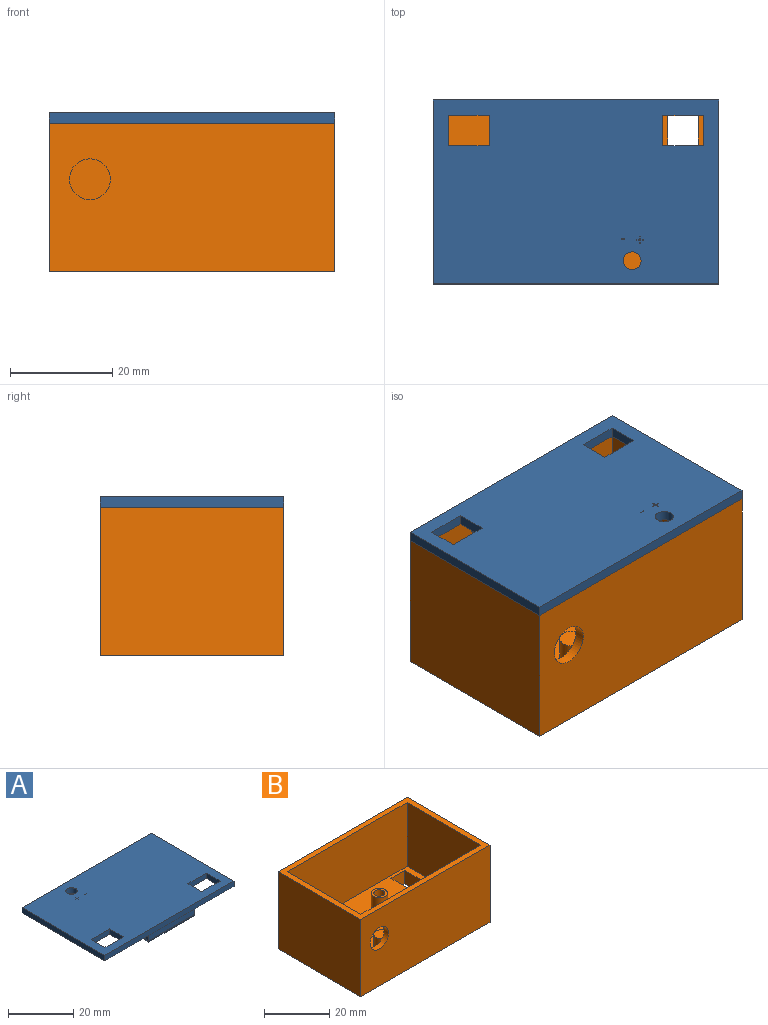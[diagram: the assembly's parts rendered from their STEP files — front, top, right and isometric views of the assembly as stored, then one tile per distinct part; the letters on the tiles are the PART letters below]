
ASSEMBLY  parts=2 mates=1
PART A: 47 faces, bbox 56x36x7 mm
  f0: plane 56x36mm, normal (0,0,1), area 1909.8mm2, adj f1,f2,f3,f4,f20,f21,f22,f23
  f1: plane 36x2mm, normal (-1,0,0), area 72mm2, adj f0,f2,f4,f5
  f2: plane 56x2mm, normal (0,-1,0), area 112mm2, adj f0,f1,f3,f5
  f3: plane 36x2mm, normal (1,0,0), area 72mm2, adj f0,f2,f4,f5
  f4: plane 56x2mm, normal (0,1,0), area 112mm2, adj f0,f1,f3,f5
  f5: plane 56x36mm, normal (0,0,-1), area 1840.4mm2, adj f1,f2,f3,f4,f6,f7,f8,f9
  f6: plane 4x2mm, normal (-1,0,0), area 8mm2, adj f5,f7,f9,f17
  f7: plane 20x4mm, normal (0,1,0), area 80mm2, adj f5,f6,f8,f18
  f8: plane 4x2mm, normal (1,0,0), area 8mm2, adj f5,f7,f9,f19
  f9: plane 20x4mm, normal (0,-1,0), area 80mm2, adj f5,f6,f8,f18
  f10: plane 15x4mm, normal (0,-1,0), area 60mm2, adj f5,f11,f13,f15
  f11: plane 4x2mm, normal (-1,0,0), area 8mm2, adj f5,f10,f12,f14
  f12: plane 15x4mm, normal (0,1,0), area 60mm2, adj f5,f11,f13,f15
  f13: plane 4x2mm, normal (1,0,0), area 8mm2, adj f5,f10,f12,f16
  f14: cylinder r=1mm len=2mm, axis (0,-1,0), area 2mm2, adj f11,f15
  f15: cylinder r=1mm len=15mm, axis (1,0,0), area 44.8mm2, adj f10,f12,f14,f16
  f16: cylinder r=1mm len=2mm, axis (0,1,0), area 2mm2, adj f13,f15
  f17: cylinder r=1mm len=2mm, axis (0,-1,0), area 2mm2, adj f6,f18
  f18: cylinder r=1mm len=20mm, axis (1,0,0), area 60.5mm2, adj f7,f9,f17,f19
  f19: cylinder r=1mm len=2mm, axis (0,1,0), area 2mm2, adj f8,f18
  f20: cylinder r=1.75mm len=3.5mm, axis (0,0,1), area 22mm2, adj f0,f5
  f21: plane 6x2mm, normal (1,0,0), area 12mm2, adj f0,f5,f22,f23
  f22: plane 8x2mm, normal (0,-1,0), area 16mm2, adj f0,f5,f21,f24
  f23: plane 8x2mm, normal (0,1,0), area 16mm2, adj f0,f5,f21,f24
  f24: plane 6x2mm, normal (-1,0,0), area 12mm2, adj f0,f5,f22,f23
  f25: plane 6x2mm, normal (1,0,0), area 12mm2, adj f0,f5,f26,f27
  f26: plane 8x2mm, normal (0,-1,0), area 16mm2, adj f0,f5,f25,f28
  f27: plane 8x2mm, normal (0,1,0), area 16mm2, adj f0,f5,f25,f28
  f28: plane 6x2mm, normal (-1,0,0), area 12mm2, adj f0,f5,f26,f27
  f29: plane 0.5x0.21mm, normal (1,0,0), area 0.1mm2, adj f0,f30,f32,f33
  f30: plane 0.67x0.5mm, normal (0,1,0), area 0.3mm2, adj f0,f29,f31,f33
  f31: plane 0.5x0.21mm, normal (-1,0,0), area 0.1mm2, adj f0,f30,f32,f33
  f32: plane 0.67x0.5mm, normal (0,-1,0), area 0.3mm2, adj f0,f29,f31,f33
  f33: plane 0.67x0.21mm, normal (0,0,1), area 0.1mm2, adj f29,f30,f31,f32
  f34: plane 0.56x0.5mm, normal (0,-1,0), area 0.3mm2, adj f0,f35,f45,f46
  f35: plane 0.58x0.5mm, normal (-1,0,0), area 0.3mm2, adj f0,f34,f36,f46
  f36: plane 0.5x0.19mm, normal (0,-1,0), area 0.1mm2, adj f0,f35,f37,f46
  f37: plane 0.58x0.5mm, normal (1,0,0), area 0.3mm2, adj f0,f36,f38,f46
  f38: plane 0.56x0.5mm, normal (0,-1,0), area 0.3mm2, adj f0,f37,f39,f46
  f39: plane 0.5x0.19mm, normal (1,0,0), area 0.1mm2, adj f0,f38,f40,f46
  f40: plane 0.56x0.5mm, normal (0,1,0), area 0.3mm2, adj f0,f39,f41,f46
  f41: plane 0.58x0.5mm, normal (1,0,0), area 0.3mm2, adj f0,f40,f42,f46
  f42: plane 0.5x0.19mm, normal (0,1,0), area 0.1mm2, adj f0,f41,f43,f46
  f43: plane 0.58x0.5mm, normal (-1,0,0), area 0.3mm2, adj f0,f42,f44,f46
  f44: plane 0.56x0.5mm, normal (0,1,0), area 0.3mm2, adj f0,f43,f45,f46
  f45: plane 0.5x0.19mm, normal (-1,0,0), area 0.1mm2, adj f0,f34,f44,f46
  f46: plane 1.35x1.3mm, normal (0,0,1), area 0.5mm2, adj f34,f35,f36,f37,f38,f39,f40,f41
PART B: 42 faces, bbox 56x36x29 mm
  f0: plane 52x32mm, normal (0,0,1), area 1525.1mm2, adj f7,f8,f9,f10,f25,f27,f29,f34
  f1: plane 56x36mm, normal (0,0,-1), area 1877.7mm2, adj f2,f3,f4,f5,f11,f12,f13,f14
  f2: plane 36x29mm, normal (-1,0,0), area 1044mm2, adj f1,f3,f5,f6
  f3: plane 56x29mm, normal (0,-1,0), area 1573.7mm2, adj f1,f2,f4,f6,f33
  f4: plane 36x29mm, normal (1,0,0), area 1044mm2, adj f1,f3,f5,f6
  f5: plane 56x29mm, normal (0,1,0), area 1624mm2, adj f1,f2,f4,f6
  f6: plane 56x36mm, normal (0,0,1), area 352mm2, adj f2,f3,f4,f5,f7,f8,f9,f10
  f7: plane 32x24mm, normal (1,0,0), area 768mm2, adj f0,f6,f8,f9
  f8: plane 52x24mm, normal (0,-1,0), area 1248mm2, adj f0,f6,f7,f10
  f9: plane 52x24mm, normal (0,1,0), area 1197.7mm2, adj f0,f6,f7,f10,f33
  f10: plane 32x24mm, normal (-1,0,0), area 768mm2, adj f0,f6,f8,f9
  f11: plane 3.35x3mm, normal (0,-1,0), area 10mm2, adj f1,f12,f16,f17
  f12: plane 3x2.9mm, normal (-0.87,-0.5,0), area 10mm2, adj f1,f11,f13,f17
  f13: plane 3x2.9mm, normal (-0.87,0.5,0), area 10mm2, adj f1,f12,f14,f17
  f14: plane 3.35x3mm, normal (0,1,0), area 10mm2, adj f1,f13,f15,f17
  f15: plane 3x2.9mm, normal (0.87,0.5,0), area 10mm2, adj f1,f14,f16,f17
  f16: plane 3x2.9mm, normal (0.87,-0.5,0), area 10mm2, adj f1,f11,f15,f17
  f17: plane 6.7x5.8mm, normal (0,0,-1), area 20.1mm2, adj f11,f12,f13,f14,f15,f16,f32
  f18: plane 3.35x3mm, normal (0,-1,0), area 10mm2, adj f1,f19,f23,f24
  f19: plane 3x2.9mm, normal (-0.87,-0.5,0), area 10mm2, adj f1,f18,f20,f24
  f20: plane 3x2.9mm, normal (-0.87,0.5,0), area 10mm2, adj f1,f19,f21,f24
  f21: plane 3.35x3mm, normal (0,1,0), area 10mm2, adj f1,f20,f22,f24
  f22: plane 3x2.9mm, normal (0.87,0.5,0), area 10mm2, adj f1,f21,f23,f24
  f23: plane 3x2.9mm, normal (0.87,-0.5,0), area 10mm2, adj f1,f18,f22,f24
  f24: plane 6.7x5.8mm, normal (0,0,-1), area 20.1mm2, adj f18,f19,f20,f21,f22,f23,f31
  f25: cylinder r=2.5mm len=5mm, axis (0,0,-1), area 78.5mm2, adj f0,f26
  f26: plane 5x5mm, normal (0,0,1), area 10.6mm2, adj f25,f32
  f27: cylinder r=2.5mm len=5mm, axis (0,0,-1), area 78.5mm2, adj f0,f28
  f28: plane 5x5mm, normal (0,0,1), area 10.6mm2, adj f27,f31
  f29: cylinder r=2.5mm len=5mm, axis (0,0,-1), area 78.5mm2, adj f0,f30
  f30: plane 5x5mm, normal (0,0,1), area 19.6mm2, adj f29
  f31: cylinder r=1.7mm len=7mm, axis (0,0,1), area 74.8mm2, adj f24,f28
  f32: cylinder r=1.7mm len=7mm, axis (0,0,1), area 74.8mm2, adj f17,f26
  f33: cylinder r=4mm len=8mm, axis (0,-1,0), area 50.3mm2, adj f3,f9
  f34: plane 6x5mm, normal (0,-1,0), area 30mm2, adj f0,f1,f35,f37
  f35: plane 8x5mm, normal (-1,0,0), area 40mm2, adj f0,f1,f34,f36
  f36: plane 6x5mm, normal (0,1,0), area 30mm2, adj f0,f1,f35,f37
  f37: plane 8x5mm, normal (1,0,0), area 40mm2, adj f0,f1,f34,f36
  f38: plane 5x4mm, normal (-1,0,0), area 20mm2, adj f0,f1,f39,f41
  f39: plane 8x5mm, normal (0,1,0), area 40mm2, adj f0,f1,f38,f40
  f40: plane 5x4mm, normal (1,0,0), area 20mm2, adj f0,f1,f39,f41
  f41: plane 8x5mm, normal (0,-1,0), area 40mm2, adj f0,f1,f38,f40
PLACE A rot(axis=(0,0,1),180deg) t=(56,36,0)mm
PLACE B t=(0,0,-29)mm
MATE slider B.f6 <-> A.f5  axis (0,0,1) through (0,0,0)mm
